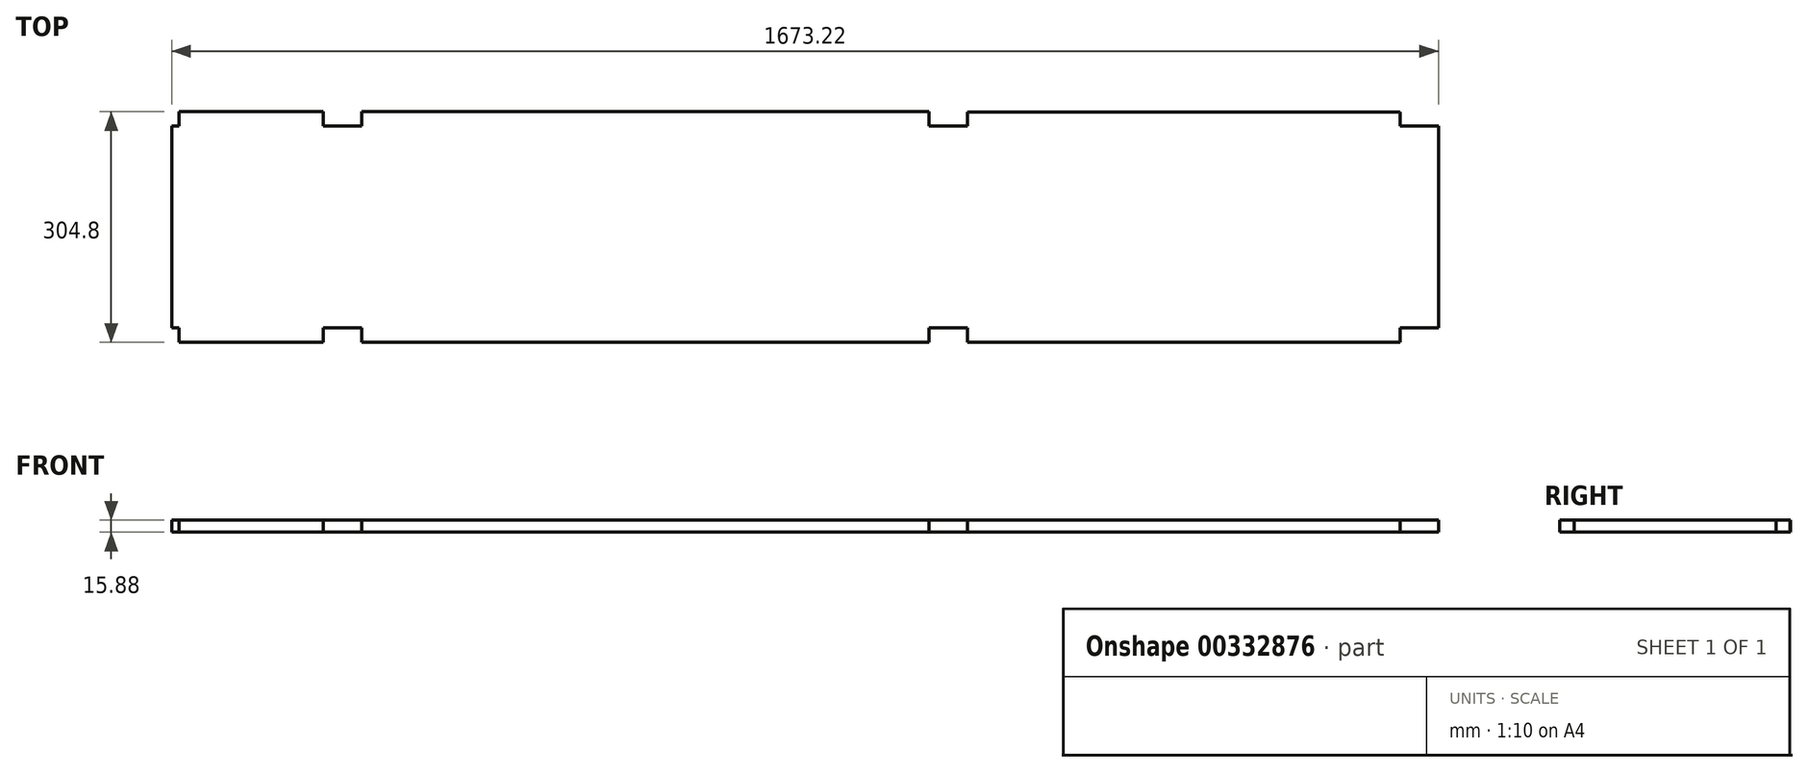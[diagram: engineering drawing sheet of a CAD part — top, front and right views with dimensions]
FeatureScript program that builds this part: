
annotation { "Feature Type Name" : "Feature", "Feature Type Description" : "" }
export const myFeature = defineFeature(function(context is Context, id is Id, definition is map)
    precondition{}
    {
        {
            var Q0;
            Q0=qCreatedBy(makeId("Top.planeOp"),FACE);
            var sketch = newSketch(context, id + "F0", { "sketchPlane" : qUnion([Q0])});
            skLineSegment(sketch, "E0.bottom", {"start": v(-685.8, -254.37) * mm, "end": v(63.5, -254.37) * mm});
            skPoint(sketch, "E0.middle", {"position": v(0, 0) * mm});
            skLineSegment(sketch, "E1.top", {"start": v(-736.6, 31.38) * mm, "end": v(-685.8, 31.38) * mm});
            skLineSegment(sketch, "E1.right", {"start": v(-685.8, 50.43) * mm, "end": v(-685.8, 31.38) * mm});
            skLineSegment(sketch, "E2.bottom", {"start": v(-685.8, -235.32) * mm, "end": v(-736.6, -235.32) * mm});
            skLineSegment(sketch, "E2.left", {"start": v(-685.8, -235.32) * mm, "end": v(-685.8, -254.37) * mm});
            skLineSegment(sketch, "E3.top", {"start": v(736.6, 31.38) * mm, "end": v(685.8, 31.38) * mm});
            skLineSegment(sketch, "E3.right", {"start": v(685.8, 50.28) * mm, "end": v(685.8, 31.38) * mm});
            skLineSegment(sketch, "E4.bottom", {"start": v(685.8, -235.32) * mm, "end": v(736.6, -235.32) * mm});
            skLineSegment(sketch, "E4.left", {"start": v(685.8, -235.32) * mm, "end": v(685.8, -254.37) * mm});
            skPoint(sketch, "E5.trimOffspring.end.orphan", {"position": v(736.6, 254.37) * mm});
            skPoint(sketch, "E6.orphan", {"position": v(736.6, -254.37) * mm});
            skPoint(sketch, "E7.orphan", {"position": v(-736.6, -254.37) * mm});
            skPoint(sketch, "E8.orphan", {"position": v(-736.6, 254.37) * mm});
            skLineSegment(sketch, "E9", {"start": v(685.8, 50.28) * mm, "end": v(114.3, 50.34) * mm});
            skLineSegment(sketch, "E10.bottom", {"start": v(63.5, 31.38) * mm, "end": v(114.3, 31.38) * mm});
            skLineSegment(sketch, "E10.left", {"start": v(63.5, 31.38) * mm, "end": v(63.5, 50.35) * mm});
            skLineSegment(sketch, "E10.right", {"start": v(114.3, 31.38) * mm, "end": v(114.3, 50.34) * mm});
            skLineSegment(sketch, "E11.bottom", {"start": v(63.5, -235.32) * mm, "end": v(114.3, -235.32) * mm});
            skLineSegment(sketch, "E11.left", {"start": v(63.5, -235.32) * mm, "end": v(63.5, -254.37) * mm});
            skLineSegment(sketch, "E11.right", {"start": v(114.3, -235.32) * mm, "end": v(114.3, -254.37) * mm});
            skLineSegment(sketch, "E12.trimOffspring", {"start": v(114.3, -254.37) * mm, "end": v(685.8, -254.37) * mm});
            skLineSegment(sketch, "E13.trimOffspring", {"start": v(63.5, 50.35) * mm, "end": v(-685.8, 50.43) * mm});
            skLineSegment(sketch, "E14", {"start": v(736.6, 31.38) * mm, "end": v(736.6, -235.32) * mm});
            skLineSegment(sketch, "E15.bottom", {"start": v(-736.6, 50.43) * mm, "end": v(-927.1, 50.43) * mm});
            skLineSegment(sketch, "E15.top", {"start": v(-736.6, -254.37) * mm, "end": v(-927.1, -254.37) * mm});
            skLineSegment(sketch, "E15.right", {"start": v(-936.62, 31.38) * mm, "end": v(-936.62, -235.32) * mm});
            skLineSegment(sketch, "E16.top", {"start": v(-936.62, -235.32) * mm, "end": v(-927.1, -235.32) * mm});
            skLineSegment(sketch, "E16.right", {"start": v(-927.1, -254.37) * mm, "end": v(-927.1, -235.32) * mm});
            skLineSegment(sketch, "E17.bottom", {"start": v(-927.1, 31.38) * mm, "end": v(-936.62, 31.38) * mm});
            skLineSegment(sketch, "E17.left", {"start": v(-927.1, 31.38) * mm, "end": v(-927.1, 50.43) * mm});
            skLineSegment(sketch, "E18.trimOffspring", {"start": v(-736.6, -235.32) * mm, "end": v(-736.6, -254.37) * mm});
            skPoint(sketch, "E19.orphan", {"position": v(-936.62, -254.37) * mm});
            skLineSegment(sketch, "E20", {"start": v(-736.6, 50.43) * mm, "end": v(-736.6, 31.38) * mm});
            skSolve(sketch);
        }
        {
            var Q0;
            Q0=qSketchRegion(id+"F0",true);
            extrude(context, id + "F1", {"entities" : qUnion([Q0]), "depth" : 15.88 * mm});
        }
    });
